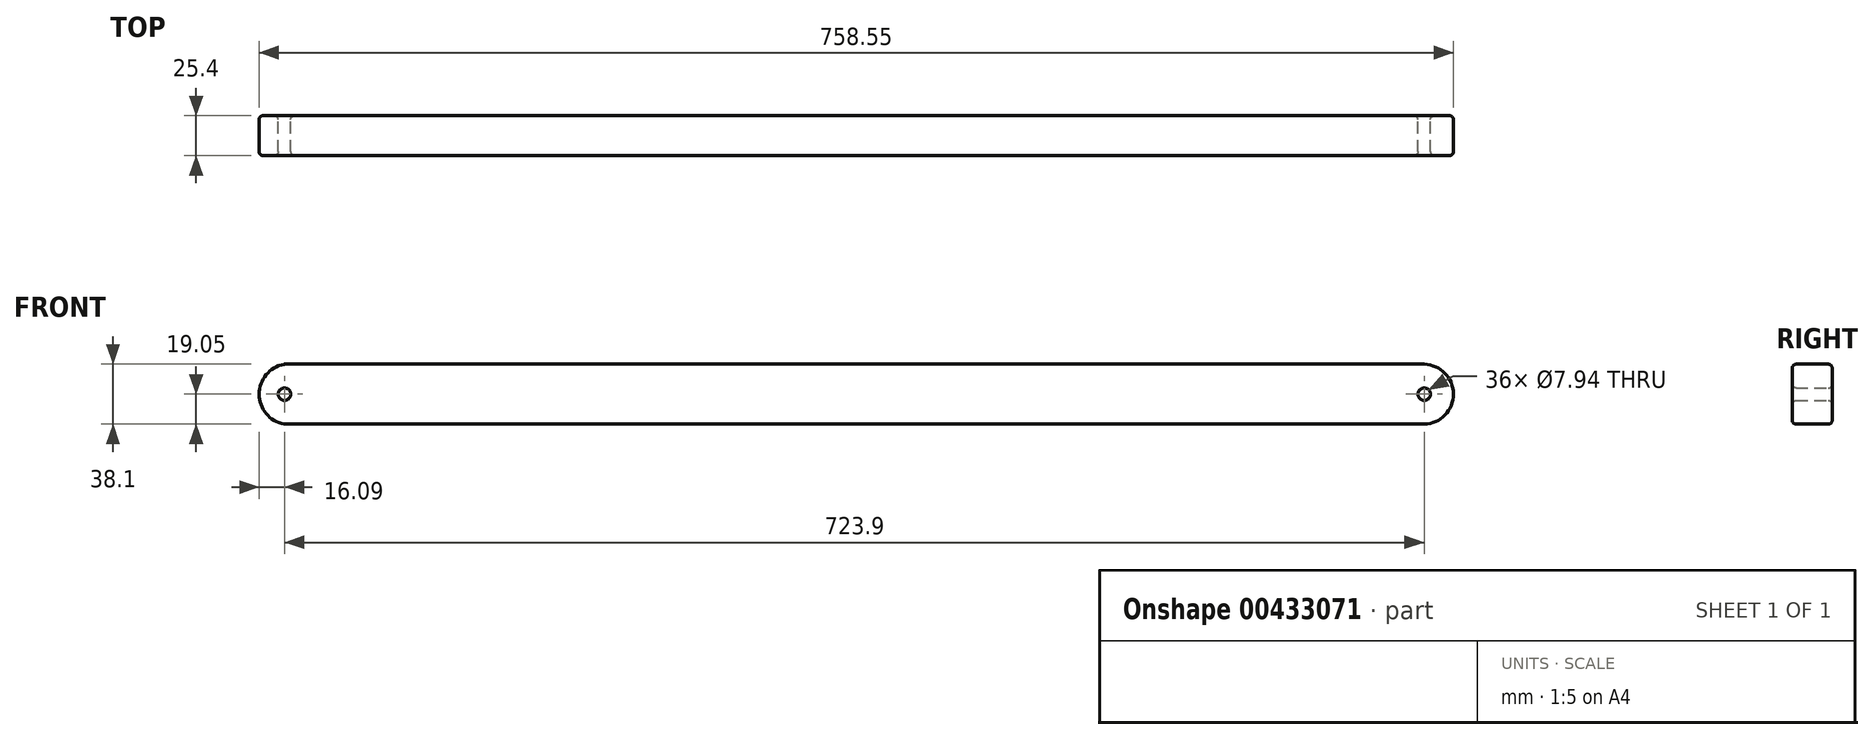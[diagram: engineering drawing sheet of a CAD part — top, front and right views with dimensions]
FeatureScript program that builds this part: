
annotation { "Feature Type Name" : "Feature", "Feature Type Description" : "" }
export const myFeature = defineFeature(function(context is Context, id is Id, definition is map)
    precondition{}
    {
        {
            var Q0;
            Q0=qCreatedBy(makeId("Front.planeOp"),FACE);
            var sketch = newSketch(context, id + "F0", { "sketchPlane" : qUnion([Q0])});
            skCircle(sketch, "E0", {"center": v(-723.9, 0) * mm, "radius": 3.97 * mm});
            skCircle(sketch, "E1", {"center": v(0, 0) * mm, "radius": 3.97 * mm});
            skLineSegment(sketch, "E2", {"start": v(-723.9, 19.05) * mm, "end": v(-723.9, -19.05) * mm});
            skLineSegment(sketch, "E3", {"start": v(0, 19.05) * mm, "end": v(0, -19.05) * mm});
            skArc(sketch, "E4", {"start": v(-723.9, 19.05) * mm, "mid": v(-739.99, 0) * mm, "end": v(-723.9, -19.05) * mm});
            skArc(sketch, "E5", {"start": v(0, -19.05) * mm, "mid": v(18.56, 0) * mm, "end": v(0, 19.05) * mm});
            skLineSegment(sketch, "E6", {"start": v(-723.9, 19.05) * mm, "end": v(0, 19.05) * mm});
            skLineSegment(sketch, "E7", {"start": v(-723.9, -19.05) * mm, "end": v(0, -19.05) * mm});
            skSolve(sketch);
        }
        {
            var Q0;
            {var subQ4=sQuery(id+"F0.wireOp",EDGE,"E4");Q0=makeQuery(id+"F0.imprint","IMPRINT",FACE,{"disambiguationData":[TD([[makeQuery(id+"F0.imprint","IMPRINT",EDGE,{"derivedFrom":subQ4}),1.0]])]});}
            var Q1;
            {var subQ0=sQuery(id+"F0.wireOp",EDGE,"E6");Q1=makeQuery(id+"F0.imprint","IMPRINT",FACE,{"disambiguationData":[TD([[makeQuery(id+"F0.imprint","IMPRINT",EDGE,{"derivedFrom":subQ0}),-1.0]])]});}
            var Q2;
            {var subQ4=sQuery(id+"F0.wireOp",EDGE,"E5");Q2=makeQuery(id+"F0.imprint","IMPRINT",FACE,{"disambiguationData":[TD([[makeQuery(id+"F0.imprint","IMPRINT",EDGE,{"derivedFrom":subQ4}),1.0]])]});}
            var Q3;
            {var subQ0=sQuery(id+"F0.wireOp",EDGE,"E7");Q3=makeQuery(id+"F0.imprint","IMPRINT",FACE,{"disambiguationData":[TD([[makeQuery(id+"F0.imprint","IMPRINT",EDGE,{"derivedFrom":subQ0}),1.0]])]});}
            extrude(context, id + "F1", {"entities" : qUnion([Q0, Q1, Q2, Q3]), "depth" : 25.4 * mm});
        }
        {
            var Q0;
            Q0=makeQuery(id+"F1.opExtrude","CAP_EDGE",EDGE,{"disambiguationData":[OSD([sQuery(id+"F0.wireOp",EDGE,"E6")])],"isStart":false});
            var Q1;
            Q1=makeQuery(id+"F1.opExtrude","SWEPT_FACE",FACE,{"disambiguationData":[OSD([sQuery(id+"F0.wireOp",EDGE,"E4")])]});
            var Q2;
            Q2=makeQuery(id+"F1.opExtrude","CAP_FACE",FACE,{"disambiguationData":[OSD([sQuery(id+"F0.wireOp",EDGE,"E0"),sQuery(id+"F0.wireOp",EDGE,"E1"),sQuery(id+"F0.wireOp",EDGE,"E4"),sQuery(id+"F0.wireOp",EDGE,"E5"),sQuery(id+"F0.wireOp",EDGE,"E6"),sQuery(id+"F0.wireOp",EDGE,"E7")])],"isStart":false});
            var Q3;
            Q3=makeQuery(id+"F1.opExtrude","CAP_FACE",FACE,{"disambiguationData":[OSD([sQuery(id+"F0.wireOp",EDGE,"E0"),sQuery(id+"F0.wireOp",EDGE,"E1"),sQuery(id+"F0.wireOp",EDGE,"E4"),sQuery(id+"F0.wireOp",EDGE,"E5"),sQuery(id+"F0.wireOp",EDGE,"E6"),sQuery(id+"F0.wireOp",EDGE,"E7")])],"isStart":true});
            var Q4;
            Q4=makeQuery(id+"F1.opExtrude","SWEPT_FACE",FACE,{"disambiguationData":[OSD([sQuery(id+"F0.wireOp",EDGE,"E0")])]});
            var Q5;
            Q5=makeQuery(id+"F1.opExtrude","CAP_EDGE",EDGE,{"disambiguationData":[OSD([sQuery(id+"F0.wireOp",EDGE,"E7")])],"isStart":false});
            var Q6;
            Q6=makeQuery(id+"F1.opExtrude","SWEPT_FACE",FACE,{"disambiguationData":[OSD([sQuery(id+"F0.wireOp",EDGE,"E7")])]});
            var Q7;
            Q7=makeQuery(id+"F1.opExtrude","SWEPT_FACE",FACE,{"disambiguationData":[OSD([sQuery(id+"F0.wireOp",EDGE,"E6")])]});
            var Q8;
            Q8=makeQuery(id+"F1.opExtrude","CAP_EDGE",EDGE,{"disambiguationData":[OSD([sQuery(id+"F0.wireOp",EDGE,"E6")])],"isStart":true});
            var Q9;
            Q9=makeQuery(id+"F1.opExtrude","SWEPT_FACE",FACE,{"disambiguationData":[OSD([sQuery(id+"F0.wireOp",EDGE,"E1")])]});
            var Q10;
            Q10=makeQuery(id+"F1.opExtrude","CAP_EDGE",EDGE,{"disambiguationData":[OSD([sQuery(id+"F0.wireOp",EDGE,"E0")])],"isStart":true});
            var Q11;
            Q11=makeQuery(id+"F1.opExtrude","CAP_EDGE",EDGE,{"disambiguationData":[OSD([sQuery(id+"F0.wireOp",EDGE,"E0")])],"isStart":false});
            var Q12;
            Q12=makeQuery(id+"F1.opExtrude","SWEPT_FACE",FACE,{"disambiguationData":[OSD([sQuery(id+"F0.wireOp",EDGE,"E5")])]});
            var Q13;
            Q13=makeQuery(id+"F1.opExtrude","CAP_EDGE",EDGE,{"disambiguationData":[OSD([sQuery(id+"F0.wireOp",EDGE,"E7")])],"isStart":true});
            var Q14;
            Q14=makeQuery(id+"F1.opExtrude","CAP_EDGE",EDGE,{"disambiguationData":[OSD([sQuery(id+"F0.wireOp",EDGE,"E4")])],"isStart":false});
            var Q15;
            Q15=makeQuery(id+"F1.opExtrude","CAP_EDGE",EDGE,{"disambiguationData":[OSD([sQuery(id+"F0.wireOp",EDGE,"E4")])],"isStart":true});
            var Q16;
            Q16=makeQuery(id+"F1.opExtrude","SWEPT_EDGE",EDGE,{"disambiguationData":[OSD([sQuery(id+"F0.wireOp",EDGE,"E3"),sQuery(id+"F0.wireOp",EDGE,"E5"),sQuery(id+"F0.wireOp",EDGE,"E7")])]});
            var Q17;
            Q17=makeQuery(id+"F1.opExtrude","CAP_EDGE",EDGE,{"disambiguationData":[OSD([sQuery(id+"F0.wireOp",EDGE,"E5")])],"isStart":false});
            var Q18;
            Q18=makeQuery(id+"F1.opExtrude","CAP_EDGE",EDGE,{"disambiguationData":[OSD([sQuery(id+"F0.wireOp",EDGE,"E1")])],"isStart":false});
            var Q19;
            Q19=makeQuery(id+"F1.opExtrude","SWEPT_EDGE",EDGE,{"disambiguationData":[OSD([sQuery(id+"F0.wireOp",EDGE,"E3"),sQuery(id+"F0.wireOp",EDGE,"E5"),sQuery(id+"F0.wireOp",EDGE,"E6")])]});
            var Q20;
            Q20=makeQuery(id+"F1.opExtrude","SWEPT_EDGE",EDGE,{"disambiguationData":[OSD([sQuery(id+"F0.wireOp",EDGE,"E2"),sQuery(id+"F0.wireOp",EDGE,"E4"),sQuery(id+"F0.wireOp",EDGE,"E7")])]});
            var Q21;
            Q21=makeQuery(id+"F1.opExtrude","CAP_EDGE",EDGE,{"disambiguationData":[OSD([sQuery(id+"F0.wireOp",EDGE,"E1")])],"isStart":true});
            var Q22;
            Q22=makeQuery(id+"F1.opExtrude","SWEPT_EDGE",EDGE,{"disambiguationData":[OSD([sQuery(id+"F0.wireOp",EDGE,"E2"),sQuery(id+"F0.wireOp",EDGE,"E4"),sQuery(id+"F0.wireOp",EDGE,"E6")])]});
            var Q23;
            Q23=makeQuery(id+"F1.opExtrude","CAP_EDGE",EDGE,{"disambiguationData":[OSD([sQuery(id+"F0.wireOp",EDGE,"E5")])],"isStart":true});
            fillet(context, id + "F2", {"entities" : qUnion([Q0, Q1, Q2, Q3, Q4, Q5, Q6, Q7, Q8, Q9, Q10, Q11, Q12, Q13, Q14, Q15, Q16, Q17, Q18, Q19, Q20, Q21, Q22, Q23]), "radius" : 2.54 * mm, "tangentPropagation" : true, "allowEdgeOverflow" : false});
        }
    });
